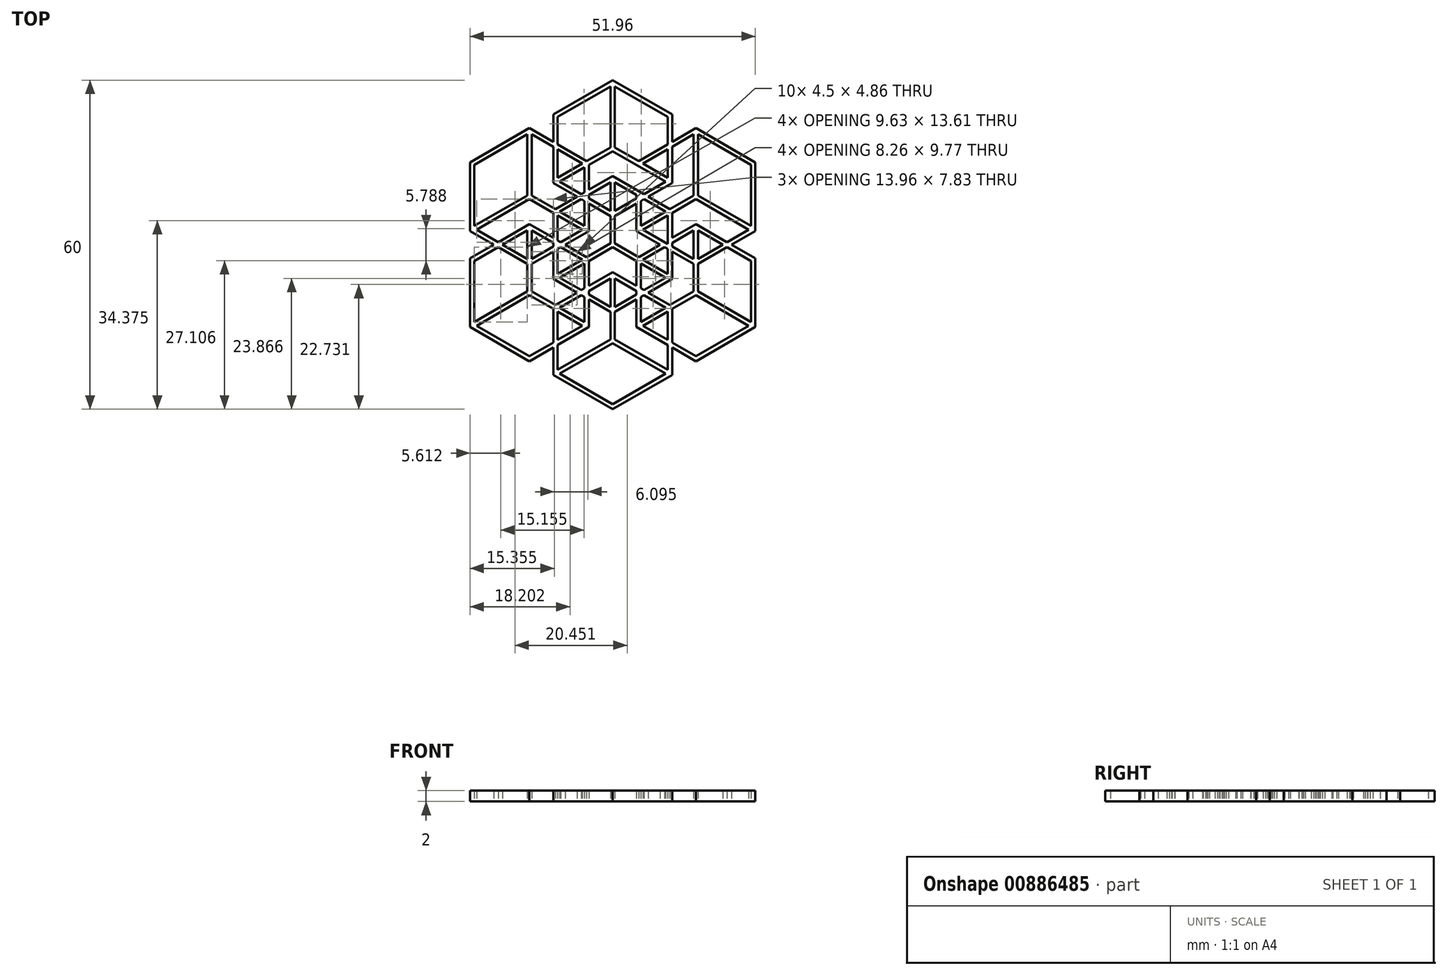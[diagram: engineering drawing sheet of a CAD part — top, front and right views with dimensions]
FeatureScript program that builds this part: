
annotation { "Feature Type Name" : "Feature", "Feature Type Description" : "" }
export const myFeature = defineFeature(function(context is Context, id is Id, definition is map)
    precondition{}
    {
        {
            var Q0;
            Q0=qCreatedBy(makeId("Top.planeOp"),FACE);
            var sketch = newSketch(context, id + "F0", { "sketchPlane" : qUnion([Q0])});
            skCircle(sketch, "E0.cCircle", {"center": v(0, 0) * mm, "radius": 30 * mm, "construction": true});
            skLineSegment(sketch, "E0.0", {"start": v(-25.98, 15) * mm, "end": v(0, 30) * mm, "construction": true});
            skLineSegment(sketch, "E0.1", {"start": v(0, 30) * mm, "end": v(25.98, 15) * mm, "construction": true});
            skLineSegment(sketch, "E0.2", {"start": v(25.98, 15) * mm, "end": v(25.98, -15) * mm, "construction": true});
            skLineSegment(sketch, "E0.3", {"start": v(25.98, -15) * mm, "end": v(0, -30) * mm, "construction": true});
            skLineSegment(sketch, "E0.4", {"start": v(0, -30) * mm, "end": v(-25.98, -15) * mm, "construction": true});
            skLineSegment(sketch, "E0.5", {"start": v(-25.98, -15) * mm, "end": v(-25.98, 15) * mm, "construction": true});
            skCircle(sketch, "E1.cCircle", {"center": v(0, -17.5) * mm, "radius": 12.5 * mm, "construction": true});
            skLineSegment(sketch, "E1.0", {"start": v(0, -30) * mm, "end": v(-10.83, -23.75) * mm});
            skLineSegment(sketch, "E1.1", {"start": v(-10.83, -23.75) * mm, "end": v(-10.83, -11.25) * mm});
            skLineSegment(sketch, "E1.2", {"start": v(-10.83, -11.25) * mm, "end": v(0, -5) * mm});
            skLineSegment(sketch, "E1.3", {"start": v(0, -5) * mm, "end": v(10.83, -11.25) * mm});
            skLineSegment(sketch, "E1.4", {"start": v(10.83, -11.25) * mm, "end": v(10.83, -23.75) * mm});
            skLineSegment(sketch, "E1.5", {"start": v(10.83, -23.75) * mm, "end": v(0, -30) * mm});
            skCircle(sketch, "E2.cCircle", {"center": v(0, -17.5) * mm, "radius": 11.58 * mm, "construction": true});
            skLineSegment(sketch, "E2.0", {"start": v(0.4, -6.15) * mm, "end": v(10.03, -11.71) * mm});
            skLineSegment(sketch, "E2.1", {"start": v(10.03, -11.71) * mm, "end": v(10.03, -22.83) * mm});
            skLineSegment(sketch, "E2.2", {"start": v(9.63, -23.52) * mm, "end": v(0, -29.08) * mm});
            skLineSegment(sketch, "E2.3", {"start": v(0, -29.08) * mm, "end": v(-9.63, -23.52) * mm});
            skLineSegment(sketch, "E2.4", {"start": v(-10.03, -22.83) * mm, "end": v(-10.03, -11.71) * mm});
            skLineSegment(sketch, "E2.5", {"start": v(-10.03, -11.71) * mm, "end": v(-0.4, -6.15) * mm});
            skLineSegment(sketch, "E3.0", {"start": v(0, -17.96) * mm, "end": v(9.63, -23.52) * mm});
            skLineSegment(sketch, "E4.0", {"start": v(0.4, -17.27) * mm, "end": v(10.03, -22.83) * mm});
            skLineSegment(sketch, "E5.0", {"start": v(-0.4, -17.27) * mm, "end": v(-10.03, -22.83) * mm});
            skLineSegment(sketch, "E6.0", {"start": v(0, -17.96) * mm, "end": v(-9.63, -23.52) * mm});
            skPoint(sketch, "E7.orphan", {"position": v(-10.03, -23.29) * mm});
            skLineSegment(sketch, "E8.trimOffspring", {"start": v(-0.4, -6.15) * mm, "end": v(-0.4, -17.27) * mm});
            skLineSegment(sketch, "E9.trimOffspring", {"start": v(0.4, -6.15) * mm, "end": v(0.4, -17.27) * mm});
            skPoint(sketch, "E10.orphan", {"position": v(0, -5.92) * mm});
            skLineSegment(sketch, "E11", {"start": v(0, -17.5) * mm, "end": v(10.83, -23.75) * mm, "construction": true});
            skLineSegment(sketch, "E12", {"start": v(0, -17.5) * mm, "end": v(-10.83, -23.75) * mm, "construction": true});
            skCircle(sketch, "E13.cCircle", {"center": v(15.16, -8.75) * mm, "radius": 12.5 * mm, "construction": true});
            skLineSegment(sketch, "E13.0", {"start": v(15.16, -21.25) * mm, "end": v(4.33, -15) * mm});
            skLineSegment(sketch, "E13.1", {"start": v(4.33, -15) * mm, "end": v(4.33, -2.5) * mm});
            skLineSegment(sketch, "E13.2", {"start": v(4.33, -2.5) * mm, "end": v(15.16, 3.75) * mm});
            skLineSegment(sketch, "E13.3", {"start": v(15.16, 3.75) * mm, "end": v(25.98, -2.5) * mm});
            skLineSegment(sketch, "E13.4", {"start": v(25.98, -2.5) * mm, "end": v(25.98, -15) * mm});
            skLineSegment(sketch, "E13.5", {"start": v(25.98, -15) * mm, "end": v(15.16, -21.25) * mm});
            skCircle(sketch, "E14.cCircle", {"center": v(15.16, -8.75) * mm, "radius": 11.58 * mm, "construction": true});
            skLineSegment(sketch, "E14.0", {"start": v(15.56, 2.6) * mm, "end": v(25.18, -2.96) * mm});
            skLineSegment(sketch, "E14.1", {"start": v(25.18, -2.96) * mm, "end": v(25.18, -14.08) * mm});
            skLineSegment(sketch, "E14.2", {"start": v(24.78, -14.77) * mm, "end": v(15.16, -20.33) * mm});
            skLineSegment(sketch, "E14.3", {"start": v(15.16, -20.33) * mm, "end": v(5.53, -14.77) * mm});
            skLineSegment(sketch, "E14.4", {"start": v(5.13, -14.08) * mm, "end": v(5.13, -2.96) * mm});
            skLineSegment(sketch, "E14.5", {"start": v(5.13, -2.96) * mm, "end": v(14.76, 2.6) * mm});
            skLineSegment(sketch, "E15.0", {"start": v(15.16, -9.21) * mm, "end": v(24.78, -14.77) * mm});
            skLineSegment(sketch, "E16.0", {"start": v(15.56, -8.52) * mm, "end": v(25.18, -14.08) * mm});
            skLineSegment(sketch, "E17.0", {"start": v(14.76, -8.52) * mm, "end": v(5.13, -14.08) * mm});
            skLineSegment(sketch, "E18.0", {"start": v(15.16, -9.21) * mm, "end": v(5.53, -14.77) * mm});
            skPoint(sketch, "E19.orphan", {"position": v(5.13, -14.54) * mm});
            skLineSegment(sketch, "E20.trimOffspring", {"start": v(14.76, 2.6) * mm, "end": v(14.76, -8.52) * mm});
            skLineSegment(sketch, "E21.trimOffspring", {"start": v(15.56, 2.6) * mm, "end": v(15.56, -8.52) * mm});
            skPoint(sketch, "E22.orphan", {"position": v(15.16, 2.83) * mm});
            skLineSegment(sketch, "E23", {"start": v(15.16, -8.75) * mm, "end": v(25.98, -15) * mm, "construction": true});
            skLineSegment(sketch, "E24", {"start": v(15.16, -8.75) * mm, "end": v(4.33, -15) * mm, "construction": true});
            skCircle(sketch, "E25.cCircle", {"center": v(-15.16, -8.75) * mm, "radius": 12.5 * mm, "construction": true});
            skLineSegment(sketch, "E25.0", {"start": v(-15.16, -21.25) * mm, "end": v(-25.98, -15) * mm});
            skLineSegment(sketch, "E25.1", {"start": v(-25.98, -15) * mm, "end": v(-25.98, -2.5) * mm});
            skLineSegment(sketch, "E25.2", {"start": v(-25.98, -2.5) * mm, "end": v(-15.16, 3.75) * mm});
            skLineSegment(sketch, "E25.3", {"start": v(-15.16, 3.75) * mm, "end": v(-4.33, -2.5) * mm});
            skLineSegment(sketch, "E25.4", {"start": v(-4.33, -2.5) * mm, "end": v(-4.33, -15) * mm});
            skLineSegment(sketch, "E25.5", {"start": v(-4.33, -15) * mm, "end": v(-15.16, -21.25) * mm});
            skCircle(sketch, "E26.cCircle", {"center": v(-15.16, -8.75) * mm, "radius": 11.58 * mm, "construction": true});
            skLineSegment(sketch, "E26.0", {"start": v(-14.76, 2.6) * mm, "end": v(-5.13, -2.96) * mm});
            skLineSegment(sketch, "E26.1", {"start": v(-5.13, -2.96) * mm, "end": v(-5.13, -14.08) * mm});
            skLineSegment(sketch, "E26.2", {"start": v(-5.53, -14.77) * mm, "end": v(-15.16, -20.33) * mm});
            skLineSegment(sketch, "E26.3", {"start": v(-15.16, -20.33) * mm, "end": v(-24.78, -14.77) * mm});
            skLineSegment(sketch, "E26.4", {"start": v(-25.18, -14.08) * mm, "end": v(-25.18, -2.96) * mm});
            skLineSegment(sketch, "E26.5", {"start": v(-25.18, -2.96) * mm, "end": v(-15.56, 2.6) * mm});
            skLineSegment(sketch, "E27.0", {"start": v(-15.16, -9.21) * mm, "end": v(-5.53, -14.77) * mm});
            skLineSegment(sketch, "E28.0", {"start": v(-14.76, -8.52) * mm, "end": v(-5.13, -14.08) * mm});
            skLineSegment(sketch, "E29.0", {"start": v(-15.56, -8.52) * mm, "end": v(-25.18, -14.08) * mm});
            skLineSegment(sketch, "E30.0", {"start": v(-15.16, -9.21) * mm, "end": v(-24.78, -14.77) * mm});
            skPoint(sketch, "E31.orphan", {"position": v(-25.18, -14.54) * mm});
            skLineSegment(sketch, "E32.trimOffspring", {"start": v(-15.56, 2.6) * mm, "end": v(-15.56, -8.52) * mm});
            skLineSegment(sketch, "E33.trimOffspring", {"start": v(-14.76, 2.6) * mm, "end": v(-14.76, -8.52) * mm});
            skPoint(sketch, "E34.orphan", {"position": v(-15.16, 2.83) * mm});
            skLineSegment(sketch, "E35", {"start": v(-15.16, -8.75) * mm, "end": v(-4.33, -15) * mm, "construction": true});
            skLineSegment(sketch, "E36", {"start": v(-15.16, -8.75) * mm, "end": v(-25.98, -15) * mm, "construction": true});
            skCircle(sketch, "E37.cCircle", {"center": v(0, 17.5) * mm, "radius": 12.5 * mm, "construction": true});
            skLineSegment(sketch, "E37.0", {"start": v(0, 5) * mm, "end": v(-10.83, 11.25) * mm});
            skLineSegment(sketch, "E37.1", {"start": v(-10.83, 11.25) * mm, "end": v(-10.83, 23.75) * mm});
            skLineSegment(sketch, "E37.2", {"start": v(-10.83, 23.75) * mm, "end": v(0, 30) * mm});
            skLineSegment(sketch, "E37.3", {"start": v(0, 30) * mm, "end": v(10.83, 23.75) * mm});
            skLineSegment(sketch, "E37.4", {"start": v(10.83, 23.75) * mm, "end": v(10.83, 11.25) * mm});
            skLineSegment(sketch, "E37.5", {"start": v(10.83, 11.25) * mm, "end": v(0, 5) * mm});
            skCircle(sketch, "E38.cCircle", {"center": v(0, 17.5) * mm, "radius": 11.58 * mm, "construction": true});
            skLineSegment(sketch, "E38.0", {"start": v(0.4, 28.85) * mm, "end": v(10.03, 23.29) * mm});
            skLineSegment(sketch, "E38.1", {"start": v(10.03, 23.29) * mm, "end": v(10.03, 12.17) * mm});
            skLineSegment(sketch, "E38.2", {"start": v(9.63, 11.48) * mm, "end": v(0, 5.92) * mm});
            skLineSegment(sketch, "E38.3", {"start": v(0, 5.92) * mm, "end": v(-9.63, 11.48) * mm});
            skLineSegment(sketch, "E38.4", {"start": v(-10.03, 12.17) * mm, "end": v(-10.03, 23.29) * mm});
            skLineSegment(sketch, "E38.5", {"start": v(-10.03, 23.29) * mm, "end": v(-0.4, 28.85) * mm});
            skLineSegment(sketch, "E39.0", {"start": v(0, 17.04) * mm, "end": v(9.63, 11.48) * mm});
            skLineSegment(sketch, "E40.0", {"start": v(0.4, 17.73) * mm, "end": v(10.03, 12.17) * mm});
            skLineSegment(sketch, "E41.0", {"start": v(-0.4, 17.73) * mm, "end": v(-10.03, 12.17) * mm});
            skLineSegment(sketch, "E42.0", {"start": v(0, 17.04) * mm, "end": v(-9.63, 11.48) * mm});
            skPoint(sketch, "E43.orphan", {"position": v(-10.03, 11.71) * mm});
            skLineSegment(sketch, "E44.trimOffspring", {"start": v(-0.4, 28.85) * mm, "end": v(-0.4, 17.73) * mm});
            skLineSegment(sketch, "E45.trimOffspring", {"start": v(0.4, 28.85) * mm, "end": v(0.4, 17.73) * mm});
            skPoint(sketch, "E46.orphan", {"position": v(0, 29.08) * mm});
            skLineSegment(sketch, "E47", {"start": v(0, 17.5) * mm, "end": v(10.83, 11.25) * mm, "construction": true});
            skLineSegment(sketch, "E48", {"start": v(0, 17.5) * mm, "end": v(-10.83, 11.25) * mm, "construction": true});
            skCircle(sketch, "E49.cCircle", {"center": v(-15.16, 8.75) * mm, "radius": 12.5 * mm, "construction": true});
            skLineSegment(sketch, "E49.0", {"start": v(-15.16, -3.75) * mm, "end": v(-25.98, 2.5) * mm});
            skLineSegment(sketch, "E49.1", {"start": v(-25.98, 2.5) * mm, "end": v(-25.98, 15) * mm});
            skLineSegment(sketch, "E49.2", {"start": v(-25.98, 15) * mm, "end": v(-15.16, 21.25) * mm});
            skLineSegment(sketch, "E49.3", {"start": v(-15.16, 21.25) * mm, "end": v(-4.33, 15) * mm});
            skLineSegment(sketch, "E49.4", {"start": v(-4.33, 15) * mm, "end": v(-4.33, 2.5) * mm});
            skLineSegment(sketch, "E49.5", {"start": v(-4.33, 2.5) * mm, "end": v(-15.16, -3.75) * mm});
            skCircle(sketch, "E50.cCircle", {"center": v(-15.16, 8.75) * mm, "radius": 11.58 * mm, "construction": true});
            skLineSegment(sketch, "E50.0", {"start": v(-14.76, 20.1) * mm, "end": v(-5.13, 14.54) * mm});
            skLineSegment(sketch, "E50.1", {"start": v(-5.13, 14.54) * mm, "end": v(-5.13, 3.42) * mm});
            skLineSegment(sketch, "E50.2", {"start": v(-5.53, 2.73) * mm, "end": v(-15.16, -2.83) * mm});
            skLineSegment(sketch, "E50.3", {"start": v(-15.16, -2.83) * mm, "end": v(-24.78, 2.73) * mm});
            skLineSegment(sketch, "E50.4", {"start": v(-25.18, 3.42) * mm, "end": v(-25.18, 14.54) * mm});
            skLineSegment(sketch, "E50.5", {"start": v(-25.18, 14.54) * mm, "end": v(-15.56, 20.1) * mm});
            skLineSegment(sketch, "E51.0", {"start": v(-15.16, 8.29) * mm, "end": v(-5.53, 2.73) * mm});
            skLineSegment(sketch, "E52.0", {"start": v(-14.76, 8.98) * mm, "end": v(-5.13, 3.42) * mm});
            skLineSegment(sketch, "E53.0", {"start": v(-15.56, 8.98) * mm, "end": v(-25.18, 3.42) * mm});
            skLineSegment(sketch, "E54.0", {"start": v(-15.16, 8.29) * mm, "end": v(-24.78, 2.73) * mm});
            skPoint(sketch, "E55.orphan", {"position": v(-25.18, 2.96) * mm});
            skLineSegment(sketch, "E56.trimOffspring", {"start": v(-15.56, 20.1) * mm, "end": v(-15.56, 8.98) * mm});
            skLineSegment(sketch, "E57.trimOffspring", {"start": v(-14.76, 20.1) * mm, "end": v(-14.76, 8.98) * mm});
            skPoint(sketch, "E58.orphan", {"position": v(-15.16, 20.33) * mm});
            skLineSegment(sketch, "E59", {"start": v(-15.16, 8.75) * mm, "end": v(-4.33, 2.5) * mm, "construction": true});
            skLineSegment(sketch, "E60", {"start": v(-15.16, 8.75) * mm, "end": v(-25.98, 2.5) * mm, "construction": true});
            skCircle(sketch, "E61.cCircle", {"center": v(15.16, 8.75) * mm, "radius": 12.5 * mm, "construction": true});
            skLineSegment(sketch, "E61.0", {"start": v(15.16, -3.75) * mm, "end": v(4.33, 2.5) * mm});
            skLineSegment(sketch, "E61.1", {"start": v(4.33, 2.5) * mm, "end": v(4.33, 15) * mm});
            skLineSegment(sketch, "E61.2", {"start": v(4.33, 15) * mm, "end": v(15.16, 21.25) * mm});
            skLineSegment(sketch, "E61.3", {"start": v(15.16, 21.25) * mm, "end": v(25.98, 15) * mm});
            skLineSegment(sketch, "E61.4", {"start": v(25.98, 15) * mm, "end": v(25.98, 2.5) * mm});
            skLineSegment(sketch, "E61.5", {"start": v(25.98, 2.5) * mm, "end": v(15.16, -3.75) * mm});
            skCircle(sketch, "E62.cCircle", {"center": v(15.16, 8.75) * mm, "radius": 11.58 * mm, "construction": true});
            skLineSegment(sketch, "E62.0", {"start": v(15.56, 20.1) * mm, "end": v(25.18, 14.54) * mm});
            skLineSegment(sketch, "E62.1", {"start": v(25.18, 14.54) * mm, "end": v(25.18, 3.42) * mm});
            skLineSegment(sketch, "E62.2", {"start": v(24.78, 2.73) * mm, "end": v(15.16, -2.83) * mm});
            skLineSegment(sketch, "E62.3", {"start": v(15.16, -2.83) * mm, "end": v(5.53, 2.73) * mm});
            skLineSegment(sketch, "E62.4", {"start": v(5.13, 3.42) * mm, "end": v(5.13, 14.54) * mm});
            skLineSegment(sketch, "E62.5", {"start": v(5.13, 14.54) * mm, "end": v(14.76, 20.1) * mm});
            skLineSegment(sketch, "E63.0", {"start": v(15.16, 8.29) * mm, "end": v(24.78, 2.73) * mm});
            skLineSegment(sketch, "E64.0", {"start": v(15.56, 8.98) * mm, "end": v(25.18, 3.42) * mm});
            skLineSegment(sketch, "E65.0", {"start": v(14.76, 8.98) * mm, "end": v(5.13, 3.42) * mm});
            skLineSegment(sketch, "E66.0", {"start": v(15.16, 8.29) * mm, "end": v(5.53, 2.73) * mm});
            skPoint(sketch, "E67.orphan", {"position": v(5.13, 2.96) * mm});
            skLineSegment(sketch, "E68.trimOffspring", {"start": v(14.76, 20.1) * mm, "end": v(14.76, 8.98) * mm});
            skLineSegment(sketch, "E69.trimOffspring", {"start": v(15.56, 20.1) * mm, "end": v(15.56, 8.98) * mm});
            skPoint(sketch, "E70.orphan", {"position": v(15.16, 20.33) * mm});
            skLineSegment(sketch, "E71", {"start": v(15.16, 8.75) * mm, "end": v(25.98, 2.5) * mm, "construction": true});
            skLineSegment(sketch, "E72", {"start": v(15.16, 8.75) * mm, "end": v(4.33, 2.5) * mm, "construction": true});
            skCircle(sketch, "E73.cCircle", {"center": v(0, 0) * mm, "radius": 12.5 * mm, "construction": true});
            skLineSegment(sketch, "E73.0", {"start": v(0, -12.5) * mm, "end": v(-10.83, -6.25) * mm});
            skLineSegment(sketch, "E73.1", {"start": v(-10.83, -6.25) * mm, "end": v(-10.83, 6.25) * mm});
            skLineSegment(sketch, "E73.2", {"start": v(-10.83, 6.25) * mm, "end": v(0, 12.5) * mm});
            skLineSegment(sketch, "E73.3", {"start": v(0, 12.5) * mm, "end": v(10.83, 6.25) * mm});
            skLineSegment(sketch, "E73.4", {"start": v(10.83, 6.25) * mm, "end": v(10.83, -6.25) * mm});
            skLineSegment(sketch, "E73.5", {"start": v(10.83, -6.25) * mm, "end": v(0, -12.5) * mm});
            skCircle(sketch, "E74.cCircle", {"center": v(0, 0) * mm, "radius": 11.58 * mm, "construction": true});
            skLineSegment(sketch, "E74.0", {"start": v(0.4, 11.35) * mm, "end": v(10.03, 5.79) * mm});
            skLineSegment(sketch, "E74.1", {"start": v(10.03, 5.79) * mm, "end": v(10.03, -5.33) * mm});
            skLineSegment(sketch, "E74.2", {"start": v(9.63, -6.02) * mm, "end": v(0, -11.58) * mm});
            skLineSegment(sketch, "E74.3", {"start": v(0, -11.58) * mm, "end": v(-9.63, -6.02) * mm});
            skLineSegment(sketch, "E74.4", {"start": v(-10.03, -5.33) * mm, "end": v(-10.03, 5.79) * mm});
            skLineSegment(sketch, "E74.5", {"start": v(-10.03, 5.79) * mm, "end": v(-0.4, 11.35) * mm});
            skLineSegment(sketch, "E75.0", {"start": v(0, -0.46) * mm, "end": v(9.63, -6.02) * mm});
            skLineSegment(sketch, "E76.0", {"start": v(0.4, 0.23) * mm, "end": v(10.03, -5.33) * mm});
            skLineSegment(sketch, "E77.0", {"start": v(-0.4, 0.23) * mm, "end": v(-10.03, -5.33) * mm});
            skLineSegment(sketch, "E78.0", {"start": v(0, -0.46) * mm, "end": v(-9.63, -6.02) * mm});
            skPoint(sketch, "E79.orphan", {"position": v(-10.03, -5.79) * mm});
            skLineSegment(sketch, "E80.trimOffspring", {"start": v(-0.4, 11.35) * mm, "end": v(-0.4, 0.23) * mm});
            skLineSegment(sketch, "E81.trimOffspring", {"start": v(0.4, 11.35) * mm, "end": v(0.4, 0.23) * mm});
            skPoint(sketch, "E82.orphan", {"position": v(0, 11.58) * mm});
            skLineSegment(sketch, "E83", {"start": v(0, 0) * mm, "end": v(10.83, -6.25) * mm, "construction": true});
            skLineSegment(sketch, "E84", {"start": v(0, 0) * mm, "end": v(-10.83, -6.25) * mm, "construction": true});
            skSolve(sketch);
        }
        {
            var Q0;
            {var subQ5=sQuery(id+"F0.wireOp",EDGE,"E25.3");var subQ6=sQuery(id+"F0.wireOp",EDGE,"E25.2");var subQ7=makeQuery(id+"F0.imprint","INTERSECT",VERTEX,{"derivedFrom":[subQ6,subQ5]});Q0=makeQuery(id+"F0.imprint","IMPRINT",FACE,{"disambiguationData":[TD([[makeQuery(id+"F0.imprint","IMPRINT",EDGE,{"disambiguationData":[TD([[subQ7,1.0]])],"derivedFrom":subQ6}),-1.0]])]});}
            var Q1;
            {var subQ3=sQuery(id+"F0.wireOp",EDGE,"E25.0");Q1=makeQuery(id+"F0.imprint","IMPRINT",FACE,{"disambiguationData":[TD([[makeQuery(id+"F0.imprint","IMPRINT",EDGE,{"derivedFrom":subQ3}),-1.0]])]});}
            var Q2;
            {var subQ1=sQuery(id+"F0.wireOp",EDGE,"E2.4");var subQ11=sQuery(id+"F0.wireOp",EDGE,"E25.5");var subQ12=makeQuery(id+"F0.imprint","INTERSECT",VERTEX,{"derivedFrom":[subQ1,subQ11]});Q2=makeQuery(id+"F0.imprint","IMPRINT",FACE,{"disambiguationData":[TD([[makeQuery(id+"F0.imprint","IMPRINT",EDGE,{"disambiguationData":[TD([[subQ12,-1.0]])],"derivedFrom":subQ1}),-1.0]])]});}
            var Q3;
            {var subQ0=sQuery(id+"F0.wireOp",EDGE,"E26.1");var subQ9=sQuery(id+"F0.wireOp",EDGE,"E1.2");var subQ11=makeQuery(id+"F0.imprint","INTERSECT",VERTEX,{"derivedFrom":[subQ9,subQ0]});Q3=makeQuery(id+"F0.imprint","IMPRINT",FACE,{"disambiguationData":[TD([[makeQuery(id+"F0.imprint","IMPRINT",EDGE,{"disambiguationData":[TD([[subQ11,-1.0]])],"derivedFrom":subQ9}),1.0]])]});}
            var Q4;
            {var subQ0=sQuery(id+"F0.wireOp",EDGE,"E50.2");var subQ1=sQuery(id+"F0.wireOp",EDGE,"E26.0");var subQ2=makeQuery(id+"F0.imprint","INTERSECT",VERTEX,{"derivedFrom":[subQ1,subQ0]});Q4=makeQuery(id+"F0.imprint","IMPRINT",FACE,{"disambiguationData":[TD([[makeQuery(id+"F0.imprint","IMPRINT",EDGE,{"disambiguationData":[TD([[subQ2,-1.0]])],"derivedFrom":subQ1}),-1.0]])]});}
            var Q5;
            {var subQ0=sQuery(id+"F0.wireOp",EDGE,"E49.0");var subQ1=sQuery(id+"F0.wireOp",EDGE,"E26.5");var subQ2=makeQuery(id+"F0.imprint","INTERSECT",VERTEX,{"derivedFrom":[subQ1,subQ0]});Q5=makeQuery(id+"F0.imprint","IMPRINT",FACE,{"disambiguationData":[TD([[makeQuery(id+"F0.imprint","IMPRINT",EDGE,{"disambiguationData":[TD([[subQ2,-1.0]])],"derivedFrom":subQ1}),-1.0]])]});}
            var Q6;
            {var subQ5=sQuery(id+"F0.wireOp",EDGE,"E32.trimOffspring");var subQ9=sQuery(id+"F0.wireOp",EDGE,"E50.3");var subQ10=makeQuery(id+"F0.imprint","INTERSECT",VERTEX,{"derivedFrom":[subQ5,subQ9]});Q6=makeQuery(id+"F0.imprint","IMPRINT",FACE,{"disambiguationData":[TD([[makeQuery(id+"F0.imprint","IMPRINT",EDGE,{"disambiguationData":[TD([[subQ10,-1.0]])],"derivedFrom":subQ5}),1.0]])]});}
            var Q7;
            {var subQ0=sQuery(id+"F0.wireOp",EDGE,"E49.0");var subQ1=sQuery(id+"F0.wireOp",EDGE,"E25.2");var subQ2=makeQuery(id+"F0.imprint","INTERSECT",VERTEX,{"derivedFrom":[subQ1,subQ0]});Q7=makeQuery(id+"F0.imprint","IMPRINT",FACE,{"disambiguationData":[TD([[makeQuery(id+"F0.imprint","IMPRINT",EDGE,{"disambiguationData":[TD([[subQ2,-1.0]])],"derivedFrom":subQ1}),-1.0]])]});}
            var Q8;
            {var subQ0=sQuery(id+"F0.wireOp",EDGE,"E50.2");var subQ1=sQuery(id+"F0.wireOp",EDGE,"E25.3");var subQ2=makeQuery(id+"F0.imprint","INTERSECT",VERTEX,{"derivedFrom":[subQ1,subQ0]});Q8=makeQuery(id+"F0.imprint","IMPRINT",FACE,{"disambiguationData":[TD([[makeQuery(id+"F0.imprint","IMPRINT",EDGE,{"disambiguationData":[TD([[subQ2,-1.0]])],"derivedFrom":subQ1}),-1.0]])]});}
            var Q9;
            {var subQ9=sQuery(id+"F0.wireOp",EDGE,"E49.1");Q9=makeQuery(id+"F0.imprint","IMPRINT",FACE,{"disambiguationData":[TD([[makeQuery(id+"F0.imprint","IMPRINT",EDGE,{"derivedFrom":subQ9}),-1.0]])]});}
            var Q10;
            {var subQ0=sQuery(id+"F0.wireOp",EDGE,"E28.0");var subQ1=sQuery(id+"F0.wireOp",EDGE,"E1.2");var subQ2=makeQuery(id+"F0.imprint","INTERSECT",VERTEX,{"derivedFrom":[subQ1,subQ0]});Q10=makeQuery(id+"F0.imprint","IMPRINT",FACE,{"disambiguationData":[TD([[makeQuery(id+"F0.imprint","IMPRINT",EDGE,{"disambiguationData":[TD([[subQ2,-1.0]])],"derivedFrom":subQ1}),-1.0]])]});}
            var Q11;
            {var subQ0=sQuery(id+"F0.wireOp",EDGE,"E26.1");var subQ1=sQuery(id+"F0.wireOp",EDGE,"E1.2");var subQ2=makeQuery(id+"F0.imprint","INTERSECT",VERTEX,{"derivedFrom":[subQ1,subQ0]});Q11=makeQuery(id+"F0.imprint","IMPRINT",FACE,{"disambiguationData":[TD([[makeQuery(id+"F0.imprint","IMPRINT",EDGE,{"disambiguationData":[TD([[subQ2,-1.0]])],"derivedFrom":subQ1}),-1.0]])]});}
            var Q12;
            {var subQ0=sQuery(id+"F0.wireOp",EDGE,"E26.2");var subQ1=sQuery(id+"F0.wireOp",EDGE,"E1.1");var subQ2=makeQuery(id+"F0.imprint","INTERSECT",VERTEX,{"derivedFrom":[subQ1,subQ0]});Q12=makeQuery(id+"F0.imprint","IMPRINT",FACE,{"disambiguationData":[TD([[makeQuery(id+"F0.imprint","IMPRINT",EDGE,{"disambiguationData":[TD([[subQ2,-1.0]])],"derivedFrom":subQ1}),-1.0]])]});}
            var Q13;
            {var subQ7=sQuery(id+"F0.wireOp",EDGE,"E1.2");var subQ8=sQuery(id+"F0.wireOp",EDGE,"E1.1");var subQ9=makeQuery(id+"F0.imprint","INTERSECT",VERTEX,{"derivedFrom":[subQ8,subQ7]});Q13=makeQuery(id+"F0.imprint","IMPRINT",FACE,{"disambiguationData":[TD([[makeQuery(id+"F0.imprint","IMPRINT",EDGE,{"disambiguationData":[TD([[subQ9,1.0]])],"derivedFrom":subQ8}),-1.0]])]});}
            var Q14;
            {var subQ17=sQuery(id+"F0.wireOp",EDGE,"E1.0");Q14=makeQuery(id+"F0.imprint","IMPRINT",FACE,{"disambiguationData":[TD([[makeQuery(id+"F0.imprint","IMPRINT",EDGE,{"derivedFrom":subQ17}),-1.0]])]});}
            var Q15;
            {var subQ0=sQuery(id+"F0.wireOp",EDGE,"E25.5");var subQ1=sQuery(id+"F0.wireOp",EDGE,"E1.1");var subQ2=makeQuery(id+"F0.imprint","INTERSECT",VERTEX,{"derivedFrom":[subQ1,subQ0]});Q15=makeQuery(id+"F0.imprint","IMPRINT",FACE,{"disambiguationData":[TD([[makeQuery(id+"F0.imprint","IMPRINT",EDGE,{"disambiguationData":[TD([[subQ2,-1.0]])],"derivedFrom":subQ1}),-1.0]])]});}
            var Q16;
            {var subQ5=sQuery(id+"F0.wireOp",EDGE,"E37.1");var subQ6=sQuery(id+"F0.wireOp",EDGE,"E37.0");var subQ7=makeQuery(id+"F0.imprint","INTERSECT",VERTEX,{"derivedFrom":[subQ6,subQ5]});Q16=makeQuery(id+"F0.imprint","IMPRINT",FACE,{"disambiguationData":[TD([[makeQuery(id+"F0.imprint","IMPRINT",EDGE,{"disambiguationData":[TD([[subQ7,1.0]])],"derivedFrom":subQ6}),-1.0]])]});}
            var Q17;
            {var subQ0=sQuery(id+"F0.wireOp",EDGE,"E49.4");var subQ1=sQuery(id+"F0.wireOp",EDGE,"E37.0");var subQ2=makeQuery(id+"F0.imprint","INTERSECT",VERTEX,{"derivedFrom":[subQ1,subQ0]});Q17=makeQuery(id+"F0.imprint","IMPRINT",FACE,{"disambiguationData":[TD([[makeQuery(id+"F0.imprint","IMPRINT",EDGE,{"disambiguationData":[TD([[subQ2,-1.0]])],"derivedFrom":subQ1}),-1.0]])]});}
            var Q18;
            {var subQ0=sQuery(id+"F0.wireOp",EDGE,"E49.4");var subQ1=sQuery(id+"F0.wireOp",EDGE,"E38.3");var subQ2=makeQuery(id+"F0.imprint","INTERSECT",VERTEX,{"derivedFrom":[subQ1,subQ0]});Q18=makeQuery(id+"F0.imprint","IMPRINT",FACE,{"disambiguationData":[TD([[makeQuery(id+"F0.imprint","IMPRINT",EDGE,{"disambiguationData":[TD([[subQ2,-1.0]])],"derivedFrom":subQ1}),-1.0]])]});}
            var Q19;
            {var subQ0=sQuery(id+"F0.wireOp",EDGE,"E50.0");var subQ1=sQuery(id+"F0.wireOp",EDGE,"E38.4");var subQ2=makeQuery(id+"F0.imprint","INTERSECT",VERTEX,{"derivedFrom":[subQ1,subQ0]});Q19=makeQuery(id+"F0.imprint","IMPRINT",FACE,{"disambiguationData":[TD([[makeQuery(id+"F0.imprint","IMPRINT",EDGE,{"disambiguationData":[TD([[subQ2,-1.0]])],"derivedFrom":subQ1}),-1.0]])]});}
            var Q20;
            {var subQ0=sQuery(id+"F0.wireOp",EDGE,"E49.3");var subQ1=sQuery(id+"F0.wireOp",EDGE,"E37.1");var subQ2=makeQuery(id+"F0.imprint","INTERSECT",VERTEX,{"derivedFrom":[subQ1,subQ0]});Q20=makeQuery(id+"F0.imprint","IMPRINT",FACE,{"disambiguationData":[TD([[makeQuery(id+"F0.imprint","IMPRINT",EDGE,{"disambiguationData":[TD([[subQ2,1.0]])],"derivedFrom":subQ1}),-1.0]])]});}
            var Q21;
            {var subQ1=sQuery(id+"F0.wireOp",EDGE,"E49.3");var subQ8=sQuery(id+"F0.wireOp",EDGE,"E41.0");var subQ10=makeQuery(id+"F0.imprint","INTERSECT",VERTEX,{"derivedFrom":[subQ8,subQ1]});Q21=makeQuery(id+"F0.imprint","IMPRINT",FACE,{"disambiguationData":[TD([[makeQuery(id+"F0.imprint","IMPRINT",EDGE,{"disambiguationData":[TD([[subQ10,-1.0]])],"derivedFrom":subQ8}),1.0]])]});}
            var Q22;
            {var subQ21=sQuery(id+"F0.wireOp",EDGE,"E37.2");Q22=makeQuery(id+"F0.imprint","IMPRINT",FACE,{"disambiguationData":[TD([[makeQuery(id+"F0.imprint","IMPRINT",EDGE,{"derivedFrom":subQ21}),-1.0]])]});}
            var Q23;
            {var subQ5=sQuery(id+"F0.wireOp",EDGE,"E37.0");var subQ7=sQuery(id+"F0.wireOp",EDGE,"E37.5");var subQ8=makeQuery(id+"F0.imprint","INTERSECT",VERTEX,{"derivedFrom":[subQ5,subQ7]});Q23=makeQuery(id+"F0.imprint","IMPRINT",FACE,{"disambiguationData":[TD([[makeQuery(id+"F0.imprint","IMPRINT",EDGE,{"disambiguationData":[TD([[subQ8,-1.0]])],"derivedFrom":subQ5}),-1.0]])]});}
            var Q24;
            {var subQ0=sQuery(id+"F0.wireOp",EDGE,"E62.4");var subQ1=sQuery(id+"F0.wireOp",EDGE,"E37.5");var subQ2=makeQuery(id+"F0.imprint","INTERSECT",VERTEX,{"derivedFrom":[subQ1,subQ0]});Q24=makeQuery(id+"F0.imprint","IMPRINT",FACE,{"disambiguationData":[TD([[makeQuery(id+"F0.imprint","IMPRINT",EDGE,{"disambiguationData":[TD([[subQ2,-1.0]])],"derivedFrom":subQ1}),-1.0]])]});}
            var Q25;
            {var subQ0=sQuery(id+"F0.wireOp",EDGE,"E62.4");var subQ1=sQuery(id+"F0.wireOp",EDGE,"E38.2");var subQ2=makeQuery(id+"F0.imprint","INTERSECT",VERTEX,{"derivedFrom":[subQ1,subQ0]});Q25=makeQuery(id+"F0.imprint","IMPRINT",FACE,{"disambiguationData":[TD([[makeQuery(id+"F0.imprint","IMPRINT",EDGE,{"disambiguationData":[TD([[subQ2,-1.0]])],"derivedFrom":subQ1}),-1.0]])]});}
            var Q26;
            {var subQ12=sQuery(id+"F0.wireOp",EDGE,"E37.5");var subQ13=sQuery(id+"F0.wireOp",EDGE,"E37.4");var subQ14=makeQuery(id+"F0.imprint","INTERSECT",VERTEX,{"derivedFrom":[subQ13,subQ12]});Q26=makeQuery(id+"F0.imprint","IMPRINT",FACE,{"disambiguationData":[TD([[makeQuery(id+"F0.imprint","IMPRINT",EDGE,{"disambiguationData":[TD([[subQ14,1.0]])],"derivedFrom":subQ13}),-1.0]])]});}
            var Q27;
            {var subQ1=sQuery(id+"F0.wireOp",EDGE,"E61.1");var subQ3=sQuery(id+"F0.wireOp",EDGE,"E39.0");var subQ4=makeQuery(id+"F0.imprint","INTERSECT",VERTEX,{"derivedFrom":[subQ3,subQ1]});Q27=makeQuery(id+"F0.imprint","IMPRINT",FACE,{"disambiguationData":[TD([[makeQuery(id+"F0.imprint","IMPRINT",EDGE,{"disambiguationData":[TD([[subQ4,-1.0]])],"derivedFrom":subQ3}),1.0]])]});}
            var Q28;
            {var subQ0=sQuery(id+"F0.wireOp",EDGE,"E61.2");var subQ1=sQuery(id+"F0.wireOp",EDGE,"E38.1");var subQ2=makeQuery(id+"F0.imprint","INTERSECT",VERTEX,{"derivedFrom":[subQ1,subQ0]});Q28=makeQuery(id+"F0.imprint","IMPRINT",FACE,{"disambiguationData":[TD([[makeQuery(id+"F0.imprint","IMPRINT",EDGE,{"disambiguationData":[TD([[subQ2,-1.0]])],"derivedFrom":subQ1}),-1.0]])]});}
            var Q29;
            {var subQ0=sQuery(id+"F0.wireOp",EDGE,"E61.3");Q29=makeQuery(id+"F0.imprint","IMPRINT",FACE,{"disambiguationData":[TD([[makeQuery(id+"F0.imprint","IMPRINT",EDGE,{"derivedFrom":subQ0}),-1.0]])]});}
            var Q30;
            {var subQ0=sQuery(id+"F0.wireOp",EDGE,"E61.2");var subQ1=sQuery(id+"F0.wireOp",EDGE,"E37.4");var subQ2=makeQuery(id+"F0.imprint","INTERSECT",VERTEX,{"derivedFrom":[subQ1,subQ0]});Q30=makeQuery(id+"F0.imprint","IMPRINT",FACE,{"disambiguationData":[TD([[makeQuery(id+"F0.imprint","IMPRINT",EDGE,{"disambiguationData":[TD([[subQ2,-1.0]])],"derivedFrom":subQ1}),-1.0]])]});}
            var Q31;
            {var subQ0=sQuery(id+"F0.wireOp",EDGE,"E61.0");var subQ1=sQuery(id+"F0.wireOp",EDGE,"E14.5");var subQ2=makeQuery(id+"F0.imprint","INTERSECT",VERTEX,{"derivedFrom":[subQ1,subQ0]});Q31=makeQuery(id+"F0.imprint","IMPRINT",FACE,{"disambiguationData":[TD([[makeQuery(id+"F0.imprint","IMPRINT",EDGE,{"disambiguationData":[TD([[subQ2,-1.0]])],"derivedFrom":subQ1}),-1.0]])]});}
            var Q32;
            {var subQ0=sQuery(id+"F0.wireOp",EDGE,"E61.0");var subQ1=sQuery(id+"F0.wireOp",EDGE,"E13.2");var subQ2=makeQuery(id+"F0.imprint","INTERSECT",VERTEX,{"derivedFrom":[subQ1,subQ0]});Q32=makeQuery(id+"F0.imprint","IMPRINT",FACE,{"disambiguationData":[TD([[makeQuery(id+"F0.imprint","IMPRINT",EDGE,{"disambiguationData":[TD([[subQ2,-1.0]])],"derivedFrom":subQ1}),-1.0]])]});}
            var Q33;
            {var subQ12=sQuery(id+"F0.wireOp",EDGE,"E13.3");var subQ13=sQuery(id+"F0.wireOp",EDGE,"E13.2");var subQ14=makeQuery(id+"F0.imprint","INTERSECT",VERTEX,{"derivedFrom":[subQ13,subQ12]});Q33=makeQuery(id+"F0.imprint","IMPRINT",FACE,{"disambiguationData":[TD([[makeQuery(id+"F0.imprint","IMPRINT",EDGE,{"disambiguationData":[TD([[subQ14,1.0]])],"derivedFrom":subQ13}),-1.0]])]});}
            var Q34;
            {var subQ3=sQuery(id+"F0.wireOp",EDGE,"E20.trimOffspring");var subQ9=sQuery(id+"F0.wireOp",EDGE,"E62.3");var subQ10=makeQuery(id+"F0.imprint","INTERSECT",VERTEX,{"derivedFrom":[subQ3,subQ9]});Q34=makeQuery(id+"F0.imprint","IMPRINT",FACE,{"disambiguationData":[TD([[makeQuery(id+"F0.imprint","IMPRINT",EDGE,{"disambiguationData":[TD([[subQ10,-1.0]])],"derivedFrom":subQ3}),1.0]])]});}
            var Q35;
            {var subQ0=sQuery(id+"F0.wireOp",EDGE,"E62.2");var subQ1=sQuery(id+"F0.wireOp",EDGE,"E14.0");var subQ2=makeQuery(id+"F0.imprint","INTERSECT",VERTEX,{"derivedFrom":[subQ1,subQ0]});Q35=makeQuery(id+"F0.imprint","IMPRINT",FACE,{"disambiguationData":[TD([[makeQuery(id+"F0.imprint","IMPRINT",EDGE,{"disambiguationData":[TD([[subQ2,-1.0]])],"derivedFrom":subQ1}),-1.0]])]});}
            var Q36;
            {var subQ0=sQuery(id+"F0.wireOp",EDGE,"E61.5");var subQ1=sQuery(id+"F0.wireOp",EDGE,"E13.3");var subQ2=makeQuery(id+"F0.imprint","INTERSECT",VERTEX,{"derivedFrom":[subQ1,subQ0]});Q36=makeQuery(id+"F0.imprint","IMPRINT",FACE,{"disambiguationData":[TD([[makeQuery(id+"F0.imprint","IMPRINT",EDGE,{"disambiguationData":[TD([[subQ2,1.0]])],"derivedFrom":subQ1}),-1.0]])]});}
            var Q37;
            {var subQ14=sQuery(id+"F0.wireOp",EDGE,"E13.4");Q37=makeQuery(id+"F0.imprint","IMPRINT",FACE,{"disambiguationData":[TD([[makeQuery(id+"F0.imprint","IMPRINT",EDGE,{"derivedFrom":subQ14}),-1.0]])]});}
            var Q38;
            {var subQ3=sQuery(id+"F0.wireOp",EDGE,"E1.3");var subQ6=sQuery(id+"F0.wireOp",EDGE,"E13.1");var subQ10=makeQuery(id+"F0.imprint","INTERSECT",VERTEX,{"derivedFrom":[subQ3,subQ6]});Q38=makeQuery(id+"F0.imprint","IMPRINT",FACE,{"disambiguationData":[TD([[makeQuery(id+"F0.imprint","IMPRINT",EDGE,{"disambiguationData":[TD([[subQ10,-1.0]])],"derivedFrom":subQ3}),1.0]])]});}
            var Q39;
            {var subQ0=sQuery(id+"F0.wireOp",EDGE,"E13.1");var subQ1=sQuery(id+"F0.wireOp",EDGE,"E1.3");var subQ2=makeQuery(id+"F0.imprint","INTERSECT",VERTEX,{"derivedFrom":[subQ1,subQ0]});Q39=makeQuery(id+"F0.imprint","IMPRINT",FACE,{"disambiguationData":[TD([[makeQuery(id+"F0.imprint","IMPRINT",EDGE,{"disambiguationData":[TD([[subQ2,-1.0]])],"derivedFrom":subQ1}),-1.0]])]});}
            var Q40;
            {var subQ0=sQuery(id+"F0.wireOp",EDGE,"E14.4");var subQ1=sQuery(id+"F0.wireOp",EDGE,"E1.3");var subQ2=makeQuery(id+"F0.imprint","INTERSECT",VERTEX,{"derivedFrom":[subQ1,subQ0]});Q40=makeQuery(id+"F0.imprint","IMPRINT",FACE,{"disambiguationData":[TD([[makeQuery(id+"F0.imprint","IMPRINT",EDGE,{"disambiguationData":[TD([[subQ2,-1.0]])],"derivedFrom":subQ1}),-1.0]])]});}
            var Q41;
            {var subQ1=sQuery(id+"F0.wireOp",EDGE,"E2.0");var subQ5=sQuery(id+"F0.wireOp",EDGE,"E13.1");var subQ14=makeQuery(id+"F0.imprint","INTERSECT",VERTEX,{"derivedFrom":[subQ1,subQ5]});Q41=makeQuery(id+"F0.imprint","IMPRINT",FACE,{"disambiguationData":[TD([[makeQuery(id+"F0.imprint","IMPRINT",EDGE,{"disambiguationData":[TD([[subQ14,-1.0]])],"derivedFrom":subQ1}),-1.0]])]});}
            var Q42;
            {var subQ0=sQuery(id+"F0.wireOp",EDGE,"E18.0");var subQ1=sQuery(id+"F0.wireOp",EDGE,"E1.4");var subQ2=makeQuery(id+"F0.imprint","INTERSECT",VERTEX,{"derivedFrom":[subQ1,subQ0]});Q42=makeQuery(id+"F0.imprint","IMPRINT",FACE,{"disambiguationData":[TD([[makeQuery(id+"F0.imprint","IMPRINT",EDGE,{"disambiguationData":[TD([[subQ2,-1.0]])],"derivedFrom":subQ1}),-1.0]])]});}
            var Q43;
            {var subQ0=sQuery(id+"F0.wireOp",EDGE,"E13.0");var subQ1=sQuery(id+"F0.wireOp",EDGE,"E1.4");var subQ2=makeQuery(id+"F0.imprint","INTERSECT",VERTEX,{"derivedFrom":[subQ1,subQ0]});Q43=makeQuery(id+"F0.imprint","IMPRINT",FACE,{"disambiguationData":[TD([[makeQuery(id+"F0.imprint","IMPRINT",EDGE,{"disambiguationData":[TD([[subQ2,1.0]])],"derivedFrom":subQ1}),-1.0]])]});}
            var Q44;
            {var subQ6=sQuery(id+"F0.wireOp",EDGE,"E1.4");var subQ9=sQuery(id+"F0.wireOp",EDGE,"E1.3");var subQ10=makeQuery(id+"F0.imprint","INTERSECT",VERTEX,{"derivedFrom":[subQ9,subQ6]});Q44=makeQuery(id+"F0.imprint","IMPRINT",FACE,{"disambiguationData":[TD([[makeQuery(id+"F0.imprint","IMPRINT",EDGE,{"disambiguationData":[TD([[subQ10,1.0]])],"derivedFrom":subQ9}),-1.0]])]});}
            var Q45;
            {var subQ13=sQuery(id+"F0.wireOp",EDGE,"E74.2");var subQ14=sQuery(id+"F0.wireOp",EDGE,"E1.3");var subQ15=makeQuery(id+"F0.imprint","INTERSECT",VERTEX,{"derivedFrom":[subQ14,subQ13]});Q45=makeQuery(id+"F0.imprint","IMPRINT",FACE,{"disambiguationData":[TD([[makeQuery(id+"F0.imprint","IMPRINT",EDGE,{"disambiguationData":[TD([[subQ15,-1.0]])],"derivedFrom":subQ14}),1.0]])]});}
            var Q46;
            {var subQ0=sQuery(id+"F0.wireOp",EDGE,"E74.2");var subQ1=sQuery(id+"F0.wireOp",EDGE,"E9.trimOffspring");var subQ2=makeQuery(id+"F0.imprint","INTERSECT",VERTEX,{"derivedFrom":[subQ1,subQ0]});Q46=makeQuery(id+"F0.imprint","IMPRINT",FACE,{"disambiguationData":[TD([[makeQuery(id+"F0.imprint","IMPRINT",EDGE,{"disambiguationData":[TD([[subQ2,-1.0]])],"derivedFrom":subQ1}),1.0]])]});}
            var Q47;
            {var subQ3=sQuery(id+"F0.wireOp",EDGE,"E2.1");var subQ7=sQuery(id+"F0.wireOp",EDGE,"E2.0");var subQ8=makeQuery(id+"F0.imprint","INTERSECT",VERTEX,{"derivedFrom":[subQ7,subQ3]});Q47=makeQuery(id+"F0.imprint","IMPRINT",FACE,{"disambiguationData":[TD([[makeQuery(id+"F0.imprint","IMPRINT",EDGE,{"disambiguationData":[TD([[subQ8,1.0]])],"derivedFrom":subQ7}),-1.0]])]});}
            var Q48;
            {var subQ0=sQuery(id+"F0.wireOp",EDGE,"E73.5");var subQ1=sQuery(id+"F0.wireOp",EDGE,"E1.3");var subQ2=makeQuery(id+"F0.imprint","INTERSECT",VERTEX,{"derivedFrom":[subQ1,subQ0]});Q48=makeQuery(id+"F0.imprint","IMPRINT",FACE,{"disambiguationData":[TD([[makeQuery(id+"F0.imprint","IMPRINT",EDGE,{"disambiguationData":[TD([[subQ2,-1.0]])],"derivedFrom":subQ1}),-1.0]])]});}
            var Q49;
            {var subQ5=sQuery(id+"F0.wireOp",EDGE,"E1.3");var subQ6=sQuery(id+"F0.wireOp",EDGE,"E1.2");var subQ7=makeQuery(id+"F0.imprint","INTERSECT",VERTEX,{"derivedFrom":[subQ6,subQ5]});Q49=makeQuery(id+"F0.imprint","IMPRINT",FACE,{"disambiguationData":[TD([[makeQuery(id+"F0.imprint","IMPRINT",EDGE,{"disambiguationData":[TD([[subQ7,1.0]])],"derivedFrom":subQ6}),-1.0]])]});}
            var Q50;
            {var subQ5=sQuery(id+"F0.wireOp",EDGE,"E2.0");var subQ7=sQuery(id+"F0.wireOp",EDGE,"E74.2");var subQ9=makeQuery(id+"F0.imprint","INTERSECT",VERTEX,{"derivedFrom":[subQ5,subQ7]});Q50=makeQuery(id+"F0.imprint","IMPRINT",FACE,{"disambiguationData":[TD([[makeQuery(id+"F0.imprint","IMPRINT",EDGE,{"disambiguationData":[TD([[subQ9,-1.0]])],"derivedFrom":subQ5}),-1.0]])]});}
            var Q51;
            {var subQ1=sQuery(id+"F0.wireOp",EDGE,"E1.3");var subQ7=sQuery(id+"F0.wireOp",EDGE,"E74.2");var subQ8=makeQuery(id+"F0.imprint","INTERSECT",VERTEX,{"derivedFrom":[subQ1,subQ7]});Q51=makeQuery(id+"F0.imprint","IMPRINT",FACE,{"disambiguationData":[TD([[makeQuery(id+"F0.imprint","IMPRINT",EDGE,{"disambiguationData":[TD([[subQ8,-1.0]])],"derivedFrom":subQ1}),-1.0]])]});}
            var Q52;
            {var subQ0=sQuery(id+"F0.wireOp",EDGE,"E74.3");var subQ1=sQuery(id+"F0.wireOp",EDGE,"E8.trimOffspring");var subQ2=makeQuery(id+"F0.imprint","INTERSECT",VERTEX,{"derivedFrom":[subQ1,subQ0]});Q52=makeQuery(id+"F0.imprint","IMPRINT",FACE,{"disambiguationData":[TD([[makeQuery(id+"F0.imprint","IMPRINT",EDGE,{"disambiguationData":[TD([[subQ2,-1.0]])],"derivedFrom":subQ1}),-1.0]])]});}
            var Q53;
            {var subQ0=sQuery(id+"F0.wireOp",EDGE,"E14.4");var subQ1=sQuery(id+"F0.wireOp",EDGE,"E2.0");var subQ2=makeQuery(id+"F0.imprint","INTERSECT",VERTEX,{"derivedFrom":[subQ1,subQ0]});Q53=makeQuery(id+"F0.imprint","IMPRINT",FACE,{"disambiguationData":[TD([[makeQuery(id+"F0.imprint","IMPRINT",EDGE,{"disambiguationData":[TD([[subQ2,-1.0]])],"derivedFrom":subQ1}),-1.0]])]});}
            var Q54;
            {var subQ0=sQuery(id+"F0.wireOp",EDGE,"E74.2");var subQ1=sQuery(id+"F0.wireOp",EDGE,"E2.0");var subQ2=makeQuery(id+"F0.imprint","INTERSECT",VERTEX,{"derivedFrom":[subQ1,subQ0]});Q54=makeQuery(id+"F0.imprint","IMPRINT",FACE,{"disambiguationData":[TD([[makeQuery(id+"F0.imprint","IMPRINT",EDGE,{"disambiguationData":[TD([[subQ2,-1.0]])],"derivedFrom":subQ1}),1.0]])]});}
            var Q55;
            {var subQ5=sQuery(id+"F0.wireOp",EDGE,"E13.2");var subQ6=sQuery(id+"F0.wireOp",EDGE,"E13.1");var subQ7=makeQuery(id+"F0.imprint","INTERSECT",VERTEX,{"derivedFrom":[subQ6,subQ5]});Q55=makeQuery(id+"F0.imprint","IMPRINT",FACE,{"disambiguationData":[TD([[makeQuery(id+"F0.imprint","IMPRINT",EDGE,{"disambiguationData":[TD([[subQ7,1.0]])],"derivedFrom":subQ6}),-1.0]])]});}
            var Q56;
            {var subQ0=sQuery(id+"F0.wireOp",EDGE,"E76.0");var subQ1=sQuery(id+"F0.wireOp",EDGE,"E13.2");var subQ2=makeQuery(id+"F0.imprint","INTERSECT",VERTEX,{"derivedFrom":[subQ1,subQ0]});Q56=makeQuery(id+"F0.imprint","IMPRINT",FACE,{"disambiguationData":[TD([[makeQuery(id+"F0.imprint","IMPRINT",EDGE,{"disambiguationData":[TD([[subQ2,-1.0]])],"derivedFrom":subQ1}),-1.0]])]});}
            var Q57;
            {var subQ7=sQuery(id+"F0.wireOp",EDGE,"E8.trimOffspring");var subQ9=sQuery(id+"F0.wireOp",EDGE,"E74.3");var subQ10=makeQuery(id+"F0.imprint","INTERSECT",VERTEX,{"derivedFrom":[subQ7,subQ9]});Q57=makeQuery(id+"F0.imprint","IMPRINT",FACE,{"disambiguationData":[TD([[makeQuery(id+"F0.imprint","IMPRINT",EDGE,{"disambiguationData":[TD([[subQ10,-1.0]])],"derivedFrom":subQ7}),1.0]])]});}
            var Q58;
            {var subQ0=sQuery(id+"F0.wireOp",EDGE,"E26.1");var subQ1=sQuery(id+"F0.wireOp",EDGE,"E2.5");var subQ2=makeQuery(id+"F0.imprint","INTERSECT",VERTEX,{"derivedFrom":[subQ1,subQ0]});Q58=makeQuery(id+"F0.imprint","IMPRINT",FACE,{"disambiguationData":[TD([[makeQuery(id+"F0.imprint","IMPRINT",EDGE,{"disambiguationData":[TD([[subQ2,-1.0]])],"derivedFrom":subQ1}),-1.0]])]});}
            var Q59;
            {var subQ0=sQuery(id+"F0.wireOp",EDGE,"E74.3");var subQ1=sQuery(id+"F0.wireOp",EDGE,"E2.5");var subQ2=makeQuery(id+"F0.imprint","INTERSECT",VERTEX,{"derivedFrom":[subQ1,subQ0]});Q59=makeQuery(id+"F0.imprint","IMPRINT",FACE,{"disambiguationData":[TD([[makeQuery(id+"F0.imprint","IMPRINT",EDGE,{"disambiguationData":[TD([[subQ2,-1.0]])],"derivedFrom":subQ1}),-1.0]])]});}
            var Q60;
            {var subQ0=sQuery(id+"F0.wireOp",EDGE,"E26.1");var subQ1=sQuery(id+"F0.wireOp",EDGE,"E2.5");var subQ2=makeQuery(id+"F0.imprint","INTERSECT",VERTEX,{"derivedFrom":[subQ1,subQ0]});Q60=makeQuery(id+"F0.imprint","IMPRINT",FACE,{"disambiguationData":[TD([[makeQuery(id+"F0.imprint","IMPRINT",EDGE,{"disambiguationData":[TD([[subQ2,-1.0]])],"derivedFrom":subQ1}),1.0]])]});}
            var Q61;
            {var subQ8=sQuery(id+"F0.wireOp",EDGE,"E13.2");var subQ13=sQuery(id+"F0.wireOp",EDGE,"E13.1");var subQ19=makeQuery(id+"F0.imprint","INTERSECT",VERTEX,{"derivedFrom":[subQ13,subQ8]});Q61=makeQuery(id+"F0.imprint","IMPRINT",FACE,{"disambiguationData":[TD([[makeQuery(id+"F0.imprint","IMPRINT",EDGE,{"disambiguationData":[TD([[subQ19,1.0]])],"derivedFrom":subQ13}),1.0]])]});}
            var Q62;
            {var subQ0=sQuery(id+"F0.wireOp",EDGE,"E73.0");var subQ1=sQuery(id+"F0.wireOp",EDGE,"E2.5");var subQ2=makeQuery(id+"F0.imprint","INTERSECT",VERTEX,{"derivedFrom":[subQ1,subQ0]});Q62=makeQuery(id+"F0.imprint","IMPRINT",FACE,{"disambiguationData":[TD([[makeQuery(id+"F0.imprint","IMPRINT",EDGE,{"disambiguationData":[TD([[subQ2,-1.0]])],"derivedFrom":subQ1}),-1.0]])]});}
            var Q63;
            {var subQ0=sQuery(id+"F0.wireOp",EDGE,"E73.0");var subQ1=sQuery(id+"F0.wireOp",EDGE,"E1.2");var subQ2=makeQuery(id+"F0.imprint","INTERSECT",VERTEX,{"derivedFrom":[subQ1,subQ0]});Q63=makeQuery(id+"F0.imprint","IMPRINT",FACE,{"disambiguationData":[TD([[makeQuery(id+"F0.imprint","IMPRINT",EDGE,{"disambiguationData":[TD([[subQ2,-1.0]])],"derivedFrom":subQ1}),-1.0]])]});}
            var Q64;
            {var subQ0=sQuery(id+"F0.wireOp",EDGE,"E74.3");var subQ1=sQuery(id+"F0.wireOp",EDGE,"E1.2");var subQ2=makeQuery(id+"F0.imprint","INTERSECT",VERTEX,{"derivedFrom":[subQ1,subQ0]});Q64=makeQuery(id+"F0.imprint","IMPRINT",FACE,{"disambiguationData":[TD([[makeQuery(id+"F0.imprint","IMPRINT",EDGE,{"disambiguationData":[TD([[subQ2,-1.0]])],"derivedFrom":subQ1}),-1.0]])]});}
            var Q65;
            {var subQ12=sQuery(id+"F0.wireOp",EDGE,"E73.0");var subQ13=sQuery(id+"F0.wireOp",EDGE,"E1.2");var subQ14=makeQuery(id+"F0.imprint","INTERSECT",VERTEX,{"derivedFrom":[subQ13,subQ12]});Q65=makeQuery(id+"F0.imprint","IMPRINT",FACE,{"disambiguationData":[TD([[makeQuery(id+"F0.imprint","IMPRINT",EDGE,{"disambiguationData":[TD([[subQ14,-1.0]])],"derivedFrom":subQ13}),1.0]])]});}
            var Q66;
            {var subQ0=sQuery(id+"F0.wireOp",EDGE,"E49.5");var subQ1=sQuery(id+"F0.wireOp",EDGE,"E25.3");var subQ2=makeQuery(id+"F0.imprint","INTERSECT",VERTEX,{"derivedFrom":[subQ1,subQ0]});Q66=makeQuery(id+"F0.imprint","IMPRINT",FACE,{"disambiguationData":[TD([[makeQuery(id+"F0.imprint","IMPRINT",EDGE,{"disambiguationData":[TD([[subQ2,-1.0]])],"derivedFrom":subQ1}),-1.0]])]});}
            var Q67;
            {var subQ5=sQuery(id+"F0.wireOp",EDGE,"E25.4");var subQ6=sQuery(id+"F0.wireOp",EDGE,"E25.3");var subQ7=makeQuery(id+"F0.imprint","INTERSECT",VERTEX,{"derivedFrom":[subQ6,subQ5]});Q67=makeQuery(id+"F0.imprint","IMPRINT",FACE,{"disambiguationData":[TD([[makeQuery(id+"F0.imprint","IMPRINT",EDGE,{"disambiguationData":[TD([[subQ7,1.0]])],"derivedFrom":subQ6}),-1.0]])]});}
            var Q68;
            {var subQ0=sQuery(id+"F0.wireOp",EDGE,"E73.1");var subQ1=sQuery(id+"F0.wireOp",EDGE,"E25.3");var subQ2=makeQuery(id+"F0.imprint","INTERSECT",VERTEX,{"derivedFrom":[subQ1,subQ0]});Q68=makeQuery(id+"F0.imprint","IMPRINT",FACE,{"disambiguationData":[TD([[makeQuery(id+"F0.imprint","IMPRINT",EDGE,{"disambiguationData":[TD([[subQ2,-1.0]])],"derivedFrom":subQ1}),-1.0]])]});}
            var Q69;
            {var subQ0=sQuery(id+"F0.wireOp",EDGE,"E50.2");var subQ1=sQuery(id+"F0.wireOp",EDGE,"E26.0");var subQ2=makeQuery(id+"F0.imprint","INTERSECT",VERTEX,{"derivedFrom":[subQ1,subQ0]});Q69=makeQuery(id+"F0.imprint","IMPRINT",FACE,{"disambiguationData":[TD([[makeQuery(id+"F0.imprint","IMPRINT",EDGE,{"disambiguationData":[TD([[subQ2,-1.0]])],"derivedFrom":subQ1}),1.0]])]});}
            var Q70;
            {var subQ0=sQuery(id+"F0.wireOp",EDGE,"E73.1");var subQ1=sQuery(id+"F0.wireOp",EDGE,"E26.0");var subQ2=makeQuery(id+"F0.imprint","INTERSECT",VERTEX,{"derivedFrom":[subQ1,subQ0]});Q70=makeQuery(id+"F0.imprint","IMPRINT",FACE,{"disambiguationData":[TD([[makeQuery(id+"F0.imprint","IMPRINT",EDGE,{"disambiguationData":[TD([[subQ2,-1.0]])],"derivedFrom":subQ1}),-1.0]])]});}
            var Q71;
            {var subQ0=sQuery(id+"F0.wireOp",EDGE,"E74.4");var subQ1=sQuery(id+"F0.wireOp",EDGE,"E25.3");var subQ2=makeQuery(id+"F0.imprint","INTERSECT",VERTEX,{"derivedFrom":[subQ1,subQ0]});Q71=makeQuery(id+"F0.imprint","IMPRINT",FACE,{"disambiguationData":[TD([[makeQuery(id+"F0.imprint","IMPRINT",EDGE,{"disambiguationData":[TD([[subQ2,-1.0]])],"derivedFrom":subQ1}),-1.0]])]});}
            var Q72;
            {var subQ0=sQuery(id+"F0.wireOp",EDGE,"E73.1");var subQ1=sQuery(id+"F0.wireOp",EDGE,"E25.3");var subQ2=makeQuery(id+"F0.imprint","INTERSECT",VERTEX,{"derivedFrom":[subQ1,subQ0]});Q72=makeQuery(id+"F0.imprint","IMPRINT",FACE,{"disambiguationData":[TD([[makeQuery(id+"F0.imprint","IMPRINT",EDGE,{"disambiguationData":[TD([[subQ2,-1.0]])],"derivedFrom":subQ1}),1.0]])]});}
            var Q73;
            {var subQ0=sQuery(id+"F0.wireOp",EDGE,"E50.2");var subQ1=sQuery(id+"F0.wireOp",EDGE,"E33.trimOffspring");var subQ2=makeQuery(id+"F0.imprint","INTERSECT",VERTEX,{"derivedFrom":[subQ1,subQ0]});Q73=makeQuery(id+"F0.imprint","IMPRINT",FACE,{"disambiguationData":[TD([[makeQuery(id+"F0.imprint","IMPRINT",EDGE,{"disambiguationData":[TD([[subQ2,-1.0]])],"derivedFrom":subQ1}),1.0]])]});}
            var Q74;
            {var subQ3=sQuery(id+"F0.wireOp",EDGE,"E25.3");var subQ13=sQuery(id+"F0.wireOp",EDGE,"E50.2");var subQ14=makeQuery(id+"F0.imprint","INTERSECT",VERTEX,{"derivedFrom":[subQ3,subQ13]});Q74=makeQuery(id+"F0.imprint","IMPRINT",FACE,{"disambiguationData":[TD([[makeQuery(id+"F0.imprint","IMPRINT",EDGE,{"disambiguationData":[TD([[subQ14,-1.0]])],"derivedFrom":subQ3}),1.0]])]});}
            var Q75;
            {var subQ0=sQuery(id+"F0.wireOp",EDGE,"E74.4");var subQ1=sQuery(id+"F0.wireOp",EDGE,"E26.0");var subQ2=makeQuery(id+"F0.imprint","INTERSECT",VERTEX,{"derivedFrom":[subQ1,subQ0]});Q75=makeQuery(id+"F0.imprint","IMPRINT",FACE,{"disambiguationData":[TD([[makeQuery(id+"F0.imprint","IMPRINT",EDGE,{"disambiguationData":[TD([[subQ2,-1.0]])],"derivedFrom":subQ1}),-1.0]])]});}
            var Q76;
            {var subQ0=sQuery(id+"F0.wireOp",EDGE,"E62.3");var subQ1=sQuery(id+"F0.wireOp",EDGE,"E20.trimOffspring");var subQ2=makeQuery(id+"F0.imprint","INTERSECT",VERTEX,{"derivedFrom":[subQ1,subQ0]});Q76=makeQuery(id+"F0.imprint","IMPRINT",FACE,{"disambiguationData":[TD([[makeQuery(id+"F0.imprint","IMPRINT",EDGE,{"disambiguationData":[TD([[subQ2,-1.0]])],"derivedFrom":subQ1}),-1.0]])]});}
            var Q77;
            {var subQ1=sQuery(id+"F0.wireOp",EDGE,"E14.5");var subQ5=sQuery(id+"F0.wireOp",EDGE,"E74.1");var subQ6=makeQuery(id+"F0.imprint","INTERSECT",VERTEX,{"derivedFrom":[subQ1,subQ5]});Q77=makeQuery(id+"F0.imprint","IMPRINT",FACE,{"disambiguationData":[TD([[makeQuery(id+"F0.imprint","IMPRINT",EDGE,{"disambiguationData":[TD([[subQ6,-1.0]])],"derivedFrom":subQ1}),-1.0]])]});}
            var Q78;
            {var subQ0=sQuery(id+"F0.wireOp",EDGE,"E74.1");var subQ1=sQuery(id+"F0.wireOp",EDGE,"E14.5");var subQ2=makeQuery(id+"F0.imprint","INTERSECT",VERTEX,{"derivedFrom":[subQ1,subQ0]});Q78=makeQuery(id+"F0.imprint","IMPRINT",FACE,{"disambiguationData":[TD([[makeQuery(id+"F0.imprint","IMPRINT",EDGE,{"disambiguationData":[TD([[subQ2,-1.0]])],"derivedFrom":subQ1}),1.0]])]});}
            var Q79;
            {var subQ0=sQuery(id+"F0.wireOp",EDGE,"E62.3");var subQ1=sQuery(id+"F0.wireOp",EDGE,"E14.5");var subQ2=makeQuery(id+"F0.imprint","INTERSECT",VERTEX,{"derivedFrom":[subQ1,subQ0]});Q79=makeQuery(id+"F0.imprint","IMPRINT",FACE,{"disambiguationData":[TD([[makeQuery(id+"F0.imprint","IMPRINT",EDGE,{"disambiguationData":[TD([[subQ2,-1.0]])],"derivedFrom":subQ1}),-1.0]])]});}
            var Q80;
            {var subQ1=sQuery(id+"F0.wireOp",EDGE,"E13.2");var subQ7=sQuery(id+"F0.wireOp",EDGE,"E74.1");var subQ9=makeQuery(id+"F0.imprint","INTERSECT",VERTEX,{"derivedFrom":[subQ1,subQ7]});Q80=makeQuery(id+"F0.imprint","IMPRINT",FACE,{"disambiguationData":[TD([[makeQuery(id+"F0.imprint","IMPRINT",EDGE,{"disambiguationData":[TD([[subQ9,-1.0]])],"derivedFrom":subQ1}),-1.0]])]});}
            var Q81;
            {var subQ1=sQuery(id+"F0.wireOp",EDGE,"E61.0");var subQ12=sQuery(id+"F0.wireOp",EDGE,"E13.2");var subQ13=makeQuery(id+"F0.imprint","INTERSECT",VERTEX,{"derivedFrom":[subQ12,subQ1]});Q81=makeQuery(id+"F0.imprint","IMPRINT",FACE,{"disambiguationData":[TD([[makeQuery(id+"F0.imprint","IMPRINT",EDGE,{"disambiguationData":[TD([[subQ13,-1.0]])],"derivedFrom":subQ12}),1.0]])]});}
            var Q82;
            {var subQ0=sQuery(id+"F0.wireOp",EDGE,"E74.1");var subQ1=sQuery(id+"F0.wireOp",EDGE,"E13.2");var subQ2=makeQuery(id+"F0.imprint","INTERSECT",VERTEX,{"derivedFrom":[subQ1,subQ0]});Q82=makeQuery(id+"F0.imprint","IMPRINT",FACE,{"disambiguationData":[TD([[makeQuery(id+"F0.imprint","IMPRINT",EDGE,{"disambiguationData":[TD([[subQ2,-1.0]])],"derivedFrom":subQ1}),1.0]])]});}
            var Q83;
            {var subQ1=sQuery(id+"F0.wireOp",EDGE,"E73.3");var subQ7=sQuery(id+"F0.wireOp",EDGE,"E65.0");var subQ8=makeQuery(id+"F0.imprint","INTERSECT",VERTEX,{"derivedFrom":[subQ7,subQ1]});Q83=makeQuery(id+"F0.imprint","IMPRINT",FACE,{"disambiguationData":[TD([[makeQuery(id+"F0.imprint","IMPRINT",EDGE,{"disambiguationData":[TD([[subQ8,-1.0]])],"derivedFrom":subQ7}),1.0]])]});}
            var Q84;
            {var subQ0=sQuery(id+"F0.wireOp",EDGE,"E73.3");var subQ1=sQuery(id+"F0.wireOp",EDGE,"E37.5");var subQ2=makeQuery(id+"F0.imprint","INTERSECT",VERTEX,{"derivedFrom":[subQ1,subQ0]});Q84=makeQuery(id+"F0.imprint","IMPRINT",FACE,{"disambiguationData":[TD([[makeQuery(id+"F0.imprint","IMPRINT",EDGE,{"disambiguationData":[TD([[subQ2,-1.0]])],"derivedFrom":subQ1}),1.0]])]});}
            var Q85;
            {var subQ0=sQuery(id+"F0.wireOp",EDGE,"E73.3");var subQ1=sQuery(id+"F0.wireOp",EDGE,"E37.5");var subQ2=makeQuery(id+"F0.imprint","INTERSECT",VERTEX,{"derivedFrom":[subQ1,subQ0]});Q85=makeQuery(id+"F0.imprint","IMPRINT",FACE,{"disambiguationData":[TD([[makeQuery(id+"F0.imprint","IMPRINT",EDGE,{"disambiguationData":[TD([[subQ2,-1.0]])],"derivedFrom":subQ1}),-1.0]])]});}
            var Q86;
            {var subQ0=sQuery(id+"F0.wireOp",EDGE,"E74.0");var subQ1=sQuery(id+"F0.wireOp",EDGE,"E37.5");var subQ2=makeQuery(id+"F0.imprint","INTERSECT",VERTEX,{"derivedFrom":[subQ1,subQ0]});Q86=makeQuery(id+"F0.imprint","IMPRINT",FACE,{"disambiguationData":[TD([[makeQuery(id+"F0.imprint","IMPRINT",EDGE,{"disambiguationData":[TD([[subQ2,-1.0]])],"derivedFrom":subQ1}),-1.0]])]});}
            var Q87;
            {var subQ5=sQuery(id+"F0.wireOp",EDGE,"E38.3");var subQ6=sQuery(id+"F0.wireOp",EDGE,"E38.2");var subQ7=makeQuery(id+"F0.imprint","INTERSECT",VERTEX,{"derivedFrom":[subQ6,subQ5]});Q87=makeQuery(id+"F0.imprint","IMPRINT",FACE,{"disambiguationData":[TD([[makeQuery(id+"F0.imprint","IMPRINT",EDGE,{"disambiguationData":[TD([[subQ7,1.0]])],"derivedFrom":subQ6}),-1.0]])]});}
            var Q88;
            {var subQ0=sQuery(id+"F0.wireOp",EDGE,"E62.4");var subQ1=sQuery(id+"F0.wireOp",EDGE,"E38.2");var subQ2=makeQuery(id+"F0.imprint","INTERSECT",VERTEX,{"derivedFrom":[subQ1,subQ0]});Q88=makeQuery(id+"F0.imprint","IMPRINT",FACE,{"disambiguationData":[TD([[makeQuery(id+"F0.imprint","IMPRINT",EDGE,{"disambiguationData":[TD([[subQ2,-1.0]])],"derivedFrom":subQ1}),1.0]])]});}
            var Q89;
            {var subQ0=sQuery(id+"F0.wireOp",EDGE,"E74.0");var subQ1=sQuery(id+"F0.wireOp",EDGE,"E38.2");var subQ2=makeQuery(id+"F0.imprint","INTERSECT",VERTEX,{"derivedFrom":[subQ1,subQ0]});Q89=makeQuery(id+"F0.imprint","IMPRINT",FACE,{"disambiguationData":[TD([[makeQuery(id+"F0.imprint","IMPRINT",EDGE,{"disambiguationData":[TD([[subQ2,-1.0]])],"derivedFrom":subQ1}),-1.0]])]});}
            var Q90;
            {var subQ0=sQuery(id+"F0.wireOp",EDGE,"E73.3");var subQ1=sQuery(id+"F0.wireOp",EDGE,"E38.2");var subQ2=makeQuery(id+"F0.imprint","INTERSECT",VERTEX,{"derivedFrom":[subQ1,subQ0]});Q90=makeQuery(id+"F0.imprint","IMPRINT",FACE,{"disambiguationData":[TD([[makeQuery(id+"F0.imprint","IMPRINT",EDGE,{"disambiguationData":[TD([[subQ2,-1.0]])],"derivedFrom":subQ1}),-1.0]])]});}
            var Q91;
            {var subQ0=sQuery(id+"F0.wireOp",EDGE,"E61.1");var subQ1=sQuery(id+"F0.wireOp",EDGE,"E37.5");var subQ2=makeQuery(id+"F0.imprint","INTERSECT",VERTEX,{"derivedFrom":[subQ1,subQ0]});Q91=makeQuery(id+"F0.imprint","IMPRINT",FACE,{"disambiguationData":[TD([[makeQuery(id+"F0.imprint","IMPRINT",EDGE,{"disambiguationData":[TD([[subQ2,-1.0]])],"derivedFrom":subQ1}),-1.0]])]});}
            var Q92;
            {var subQ0=sQuery(id+"F0.wireOp",EDGE,"E80.trimOffspring");var subQ1=sQuery(id+"F0.wireOp",EDGE,"E37.0");var subQ2=makeQuery(id+"F0.imprint","INTERSECT",VERTEX,{"derivedFrom":[subQ1,subQ0]});Q92=makeQuery(id+"F0.imprint","IMPRINT",FACE,{"disambiguationData":[TD([[makeQuery(id+"F0.imprint","IMPRINT",EDGE,{"disambiguationData":[TD([[subQ2,-1.0]])],"derivedFrom":subQ1}),-1.0]])]});}
            var Q93;
            {var subQ0=sQuery(id+"F0.wireOp",EDGE,"E49.4");var subQ1=sQuery(id+"F0.wireOp",EDGE,"E42.0");var subQ2=makeQuery(id+"F0.imprint","INTERSECT",VERTEX,{"derivedFrom":[subQ1,subQ0]});Q93=makeQuery(id+"F0.imprint","IMPRINT",FACE,{"disambiguationData":[TD([[makeQuery(id+"F0.imprint","IMPRINT",EDGE,{"disambiguationData":[TD([[subQ2,-1.0]])],"derivedFrom":subQ1}),1.0]])]});}
            var Q94;
            {var subQ0=sQuery(id+"F0.wireOp",EDGE,"E74.5");var subQ1=sQuery(id+"F0.wireOp",EDGE,"E37.0");var subQ2=makeQuery(id+"F0.imprint","INTERSECT",VERTEX,{"derivedFrom":[subQ1,subQ0]});Q94=makeQuery(id+"F0.imprint","IMPRINT",FACE,{"disambiguationData":[TD([[makeQuery(id+"F0.imprint","IMPRINT",EDGE,{"disambiguationData":[TD([[subQ2,-1.0]])],"derivedFrom":subQ1}),1.0]])]});}
            var Q95;
            {var subQ1=sQuery(id+"F0.wireOp",EDGE,"E73.1");var subQ3=sQuery(id+"F0.wireOp",EDGE,"E51.0");var subQ4=makeQuery(id+"F0.imprint","INTERSECT",VERTEX,{"derivedFrom":[subQ3,subQ1]});Q95=makeQuery(id+"F0.imprint","IMPRINT",FACE,{"disambiguationData":[TD([[makeQuery(id+"F0.imprint","IMPRINT",EDGE,{"disambiguationData":[TD([[subQ4,-1.0]])],"derivedFrom":subQ3}),1.0]])]});}
            var Q96;
            {var subQ0=sQuery(id+"F0.wireOp",EDGE,"E50.1");var subQ1=sQuery(id+"F0.wireOp",EDGE,"E37.0");var subQ2=makeQuery(id+"F0.imprint","INTERSECT",VERTEX,{"derivedFrom":[subQ1,subQ0]});Q96=makeQuery(id+"F0.imprint","IMPRINT",FACE,{"disambiguationData":[TD([[makeQuery(id+"F0.imprint","IMPRINT",EDGE,{"disambiguationData":[TD([[subQ2,-1.0]])],"derivedFrom":subQ1}),-1.0]])]});}
            var Q97;
            {var subQ0=sQuery(id+"F0.wireOp",EDGE,"E50.1");var subQ1=sQuery(id+"F0.wireOp",EDGE,"E38.3");var subQ2=makeQuery(id+"F0.imprint","INTERSECT",VERTEX,{"derivedFrom":[subQ1,subQ0]});Q97=makeQuery(id+"F0.imprint","IMPRINT",FACE,{"disambiguationData":[TD([[makeQuery(id+"F0.imprint","IMPRINT",EDGE,{"disambiguationData":[TD([[subQ2,-1.0]])],"derivedFrom":subQ1}),-1.0]])]});}
            var Q98;
            {var subQ1=sQuery(id+"F0.wireOp",EDGE,"E38.3");var subQ7=sQuery(id+"F0.wireOp",EDGE,"E74.5");var subQ9=makeQuery(id+"F0.imprint","INTERSECT",VERTEX,{"derivedFrom":[subQ1,subQ7]});Q98=makeQuery(id+"F0.imprint","IMPRINT",FACE,{"disambiguationData":[TD([[makeQuery(id+"F0.imprint","IMPRINT",EDGE,{"disambiguationData":[TD([[subQ9,-1.0]])],"derivedFrom":subQ1}),-1.0]])]});}
            var Q99;
            {var subQ0=sQuery(id+"F0.wireOp",EDGE,"E74.5");var subQ1=sQuery(id+"F0.wireOp",EDGE,"E38.3");var subQ2=makeQuery(id+"F0.imprint","INTERSECT",VERTEX,{"derivedFrom":[subQ1,subQ0]});Q99=makeQuery(id+"F0.imprint","IMPRINT",FACE,{"disambiguationData":[TD([[makeQuery(id+"F0.imprint","IMPRINT",EDGE,{"disambiguationData":[TD([[subQ2,-1.0]])],"derivedFrom":subQ1}),1.0]])]});}
            var Q100;
            {var subQ1=sQuery(id+"F0.wireOp",EDGE,"E37.0");var subQ7=sQuery(id+"F0.wireOp",EDGE,"E74.5");var subQ9=makeQuery(id+"F0.imprint","INTERSECT",VERTEX,{"derivedFrom":[subQ1,subQ7]});Q100=makeQuery(id+"F0.imprint","IMPRINT",FACE,{"disambiguationData":[TD([[makeQuery(id+"F0.imprint","IMPRINT",EDGE,{"disambiguationData":[TD([[subQ9,-1.0]])],"derivedFrom":subQ1}),-1.0]])]});}
            extrude(context, id + "F1", {"entities" : qUnion([Q0, Q1, Q2, Q3, Q4, Q5, Q6, Q7, Q8, Q9, Q10, Q11, Q12, Q13, Q14, Q15, Q16, Q17, Q18, Q19, Q20, Q21, Q22, Q23, Q24, Q25, Q26, Q27, Q28, Q29, Q30, Q31, Q32, Q33, Q34, Q35, Q36, Q37, Q38, Q39, Q40, Q41, Q42, Q43, Q44, Q45, Q46, Q47, Q48, Q49, Q50, Q51, Q52, Q53, Q54, Q55, Q56, Q57, Q58, Q59, Q60, Q61, Q62, Q63, Q64, Q65, Q66, Q67, Q68, Q69, Q70, Q71, Q72, Q73, Q74, Q75, Q76, Q77, Q78, Q79, Q80, Q81, Q82, Q83, Q84, Q85, Q86, Q87, Q88, Q89, Q90, Q91, Q92, Q93, Q94, Q95, Q96, Q97, Q98, Q99, Q100]), "depth" : 2 * mm, "offsetDistance" : 25 * mm});
        }
    });
